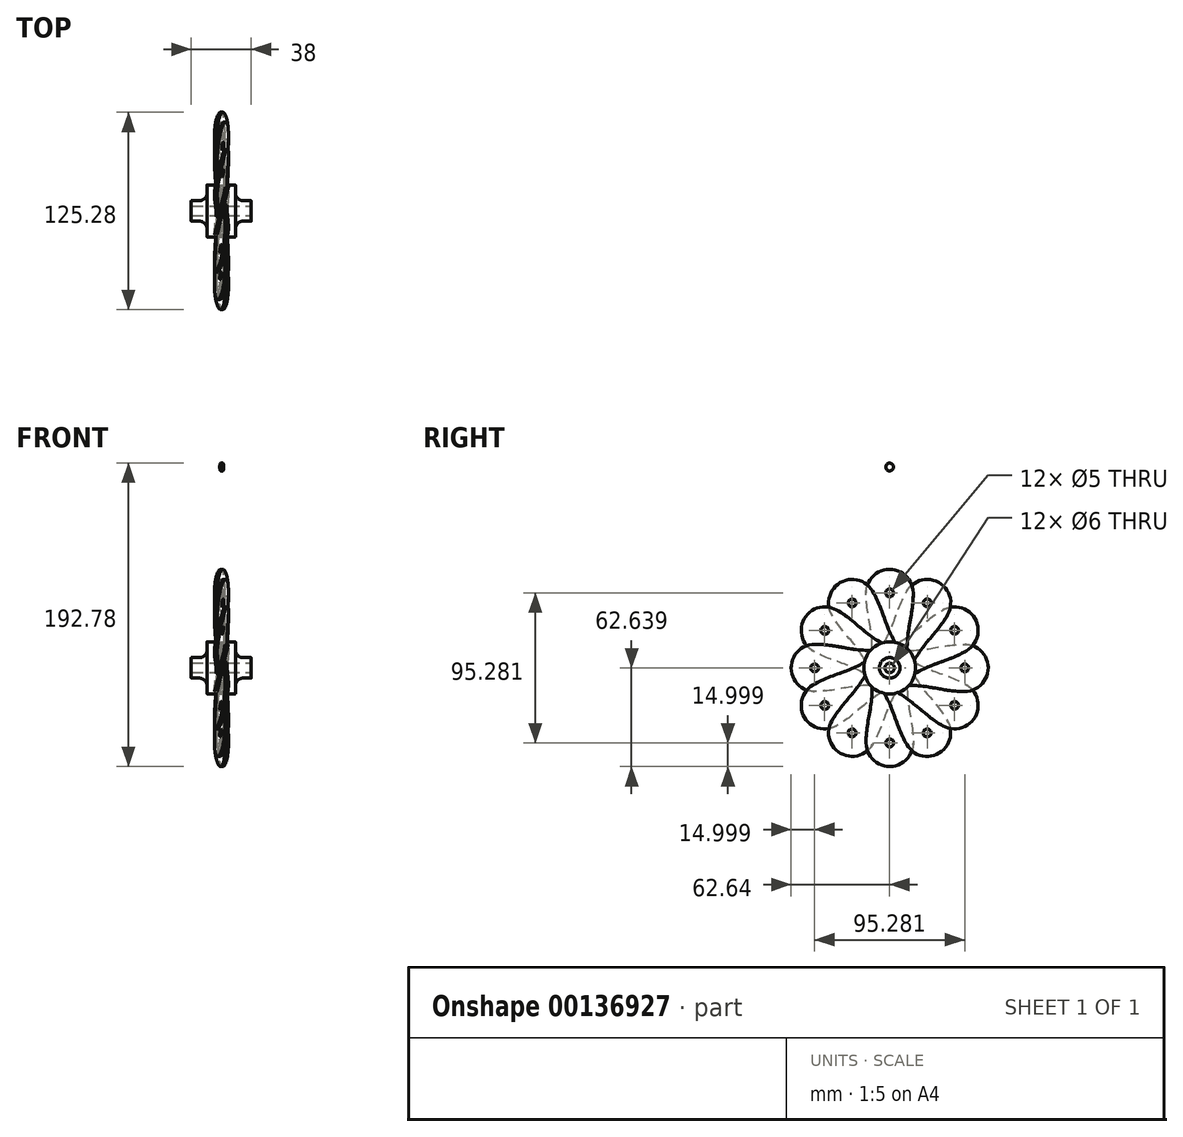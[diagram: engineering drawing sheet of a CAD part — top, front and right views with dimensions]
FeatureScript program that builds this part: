
annotation { "Feature Type Name" : "Feature", "Feature Type Description" : "" }
export const myFeature = defineFeature(function(context is Context, id is Id, definition is map)
    precondition{}
    {
        {
            var Q0;
            Q0=qCreatedBy(makeId("Right.planeOp"),FACE);
            var sketch = newSketch(context, id + "F0", { "sketchPlane" : qUnion([Q0])});
            skCircle(sketch, "E0", {"center": v(0, 0) * mm, "radius": 15 * mm});
            skCircle(sketch, "E1", {"center": v(0, -50) * mm, "radius": 12.5 * mm});
            skCircle(sketch, "E2", {"center": v(0, 80) * mm, "radius": 2.5 * mm});
            skCircle(sketch, "E3", {"center": v(0, 0) * mm, "radius": 2.5 * mm});
            skCircle(sketch, "E4.0.1.0", {"center": v(0, 25) * mm, "radius": 2.5 * mm});
            skCircle(sketch, "E4.0.2.0", {"center": v(0, 50) * mm, "radius": 2.5 * mm});
            skLineSegment(sketch, "E4.direction1", {"start": v(0, 0) * mm, "end": v(25, 0) * mm, "construction": true});
            skLineSegment(sketch, "E4.direction2", {"start": v(0, 0) * mm, "end": v(0, 25) * mm, "construction": true});
            skFitSpline(sketch, "E5", {"points": [v(-12.31, -47.84) * mm, v(-15, 0) * mm, v(-2.5, 80.18) * mm], "startDerivative": vector(26.28, 150.08) * mm, "endDerivative": vector(8.01, 113.17) * mm});
            skFitSpline(sketch, "E6.MirrorCS", {"points": [v(12.31, -47.84) * mm, v(15, 0) * mm, v(2.5, 80.18) * mm], "startDerivative": vector(-26.28, 150.08) * mm, "endDerivative": vector(-8.01, 113.17) * mm});
            skSolve(sketch);
        }
        {
            var Q0;
            {var subQ0=sQuery(id+"F0.wireOp",EDGE,"E5");var subQ1=sQuery(id+"F0.wireOp",EDGE,"E0");var subQ2=makeQuery(id+"F0.imprint","INTERSECT",VERTEX,{"derivedFrom":[subQ1,subQ0]});Q0=makeQuery(id+"F0.imprint","IMPRINT",FACE,{"disambiguationData":[TD([[makeQuery(id+"F0.imprint","IMPRINT",EDGE,{"disambiguationData":[TD([[subQ2,-1.0]])],"derivedFrom":subQ1}),-1.0]])]});}
            var Q1;
            Q1=makeQuery(id+"F0.imprint","IMPRINT",FACE,{"disambiguationData":[TD([[makeQuery(id+"F0.imprint","IMPRINT",EDGE,{"derivedFrom":sQuery(id+"F0.wireOp",EDGE,"E3")}),-1.0]])]});
            var Q2;
            Q2=makeQuery(id+"F0.imprint","IMPRINT",FACE,{"disambiguationData":[TD([[makeQuery(id+"F0.imprint","IMPRINT",EDGE,{"derivedFrom":sQuery(id+"F0.wireOp",EDGE,"E4.0.1.0")}),-1.0]])]});
            var Q3;
            {var subQ0=sQuery(id+"F0.wireOp",EDGE,"E2");var subQ1=makeQuery(id+"F0.imprint","INTERSECT",VERTEX,{"derivedFrom":[subQ0,sQuery(id+"F0.wireOp",EDGE,"E5")]});Q3=makeQuery(id+"F0.imprint","IMPRINT",FACE,{"disambiguationData":[TD([[makeQuery(id+"F0.imprint","IMPRINT",EDGE,{"disambiguationData":[TD([[subQ1,1.0]])],"derivedFrom":subQ0}),1.0]])]});}
            extrude(context, id + "F1", {"entities" : qUnion([Q0, Q1, Q2, Q3]), "depth" : 25 * mm});
        }
        {
            var Q0;
            Q0=qCreatedBy(makeId("Top.planeOp"),FACE);
            var sketch = newSketch(context, id + "F2", { "sketchPlane" : qUnion([Q0])});
            skLineSegment(sketch, "E7", {"start": v(0, -30.82) * mm, "end": v(0, 22.95) * mm});
            skLineSegment(sketch, "E8", {"start": v(0, 22.95) * mm, "end": v(12.68, 22.95) * mm});
            skLineSegment(sketch, "E9", {"start": v(-1.1, -41.33) * mm, "end": v(21.41, 54.16) * mm, "construction": true});
            skLineSegment(sketch, "E10.MirrorCS", {"start": v(15.28, 22.34) * mm, "end": v(2.6, -31.43) * mm});
            skLineSegment(sketch, "E11.MirrorCS", {"start": v(26.63, 16.67) * mm, "end": v(15.28, 22.34) * mm});
            skLineSegment(sketch, "E12", {"start": v(2.6, -31.43) * mm, "end": v(30.66, -22.66) * mm});
            skLineSegment(sketch, "E13", {"start": v(30.66, -22.66) * mm, "end": v(26.63, 16.67) * mm});
            skFitSpline(sketch, "E14", {"points": [v(0, -30.82) * mm, v(8.64, 0) * mm, v(12.68, 22.95) * mm], "startDerivative": vector(17.97, 59.07) * mm, "endDerivative": vector(7.1, 48.17) * mm});
            skSolve(sketch);
        }
        {
            var Q0;
            Q0=qSketchRegion(id+"F2",true);
            extrude(context, id + "F3", {"entities" : qUnion([Q0]), "operationType" : NewBodyOperationType.REMOVE, "oppositeDirection" : true, "depth" : 77 * mm, "hasSecondDirection" : true, "secondDirectionOppositeDirection" : false, "secondDirectionDepth" : 98.55 * mm});
        }
        {
            var Q0;
            Q0=makeQuery(id+"F3.boolean.opBoolean","INTERSECT",VERTEX,{"derivedFrom":[makeQuery(id+"F1.opExtrude","SWEPT_FACE",FACE,{"disambiguationData":[OSD([sQuery(id+"F0.wireOp",EDGE,"E1")])]}),makeQuery(id+"F1.opExtrude","SWEPT_FACE",FACE,{"disambiguationData":[OSD([sQuery(id+"F0.wireOp",EDGE,"E5")])]}),makeQuery(id+"F3.opExtrude","SWEPT_FACE",FACE,{"disambiguationData":[OSD([sQuery(id+"F2.wireOp",EDGE,"E10.MirrorCS")])]})]});
            var Q1;
            Q1=makeQuery(id+"F3.boolean.opBoolean","INTERSECT",VERTEX,{"derivedFrom":[makeQuery(id+"F1.opExtrude","SWEPT_FACE",FACE,{"disambiguationData":[OSD([sQuery(id+"F0.wireOp",EDGE,"E1")])]}),makeQuery(id+"F1.opExtrude","SWEPT_FACE",FACE,{"disambiguationData":[OSD([sQuery(id+"F0.wireOp",EDGE,"E6.MirrorCS")])]}),makeQuery(id+"F3.opExtrude","SWEPT_FACE",FACE,{"disambiguationData":[OSD([sQuery(id+"F2.wireOp",EDGE,"E10.MirrorCS")])]})]});
            var Q2;
            Q2=makeQuery(id+"F3.boolean.opBoolean","INTERSECT",VERTEX,{"derivedFrom":[makeQuery(id+"F1.opExtrude","SWEPT_FACE",FACE,{"disambiguationData":[OSD([sQuery(id+"F0.wireOp",EDGE,"E1")])]}),makeQuery(id+"F1.opExtrude","SWEPT_FACE",FACE,{"disambiguationData":[OSD([sQuery(id+"F0.wireOp",EDGE,"E6.MirrorCS")])]}),makeQuery(id+"F3.opExtrude","SWEPT_FACE",FACE,{"disambiguationData":[OSD([sQuery(id+"F2.wireOp",EDGE,"E14")])]})]});
            cPlane(context, id + "F4", {"entities" : qUnion([Q0, Q1, Q2]), "cplaneType" : CPlaneType.THREE_POINT, "offset" : 25 * mm, "width" : 150 * mm, "height" : 150 * mm});
        }
        {
            var Q0;
            Q0=qCreatedBy(id+"F4.planeOp",FACE);
            var sketch = newSketch(context, id + "F5", { "sketchPlane" : qUnion([Q0])});
            skLineSegment(sketch, "E15", {"start": v(66.32, 0) * mm, "end": v(-28.05, 0) * mm, "construction": true});
            skLineSegment(sketch, "E16", {"start": v(28, 3) * mm, "end": v(-10, 3) * mm});
            skLineSegment(sketch, "E17", {"start": v(-10, 3) * mm, "end": v(-10, 6.5) * mm});
            skLineSegment(sketch, "E18", {"start": v(-10, 6.5) * mm, "end": v(-5, 6.5) * mm});
            skLineSegment(sketch, "E19", {"start": v(0, 11.5) * mm, "end": v(0, 16.5) * mm});
            skLineSegment(sketch, "E20", {"start": v(0, 16.5) * mm, "end": v(18, 16.5) * mm});
            skLineSegment(sketch, "E21", {"start": v(18, 16.5) * mm, "end": v(18, 11.5) * mm});
            skLineSegment(sketch, "E22", {"start": v(23, 6.5) * mm, "end": v(28, 6.5) * mm});
            skLineSegment(sketch, "E23", {"start": v(28, 6.5) * mm, "end": v(28, 3) * mm});
            skPoint(sketch, "E24.visualSharp", {"position": v(18, 6.5) * mm});
            skArc(sketch, "E24.filletArc", {"start": v(18, 11.5) * mm, "mid": v(19.46, 7.96) * mm, "end": v(23, 6.5) * mm});
            skPoint(sketch, "E25.visualSharp", {"position": v(0, 6.5) * mm});
            skArc(sketch, "E25.filletArc", {"start": v(-5, 6.5) * mm, "mid": v(-1.46, 7.96) * mm, "end": v(0, 11.5) * mm});
            skSolve(sketch);
        }
        {
            var Q0;
            Q0=makeQuery(id+"F5.imprint","IMPRINT",FACE,{"disambiguationData":[TD([[makeQuery(id+"F5.imprint","IMPRINT",EDGE,{"derivedFrom":sQuery(id+"F5.wireOp",EDGE,"E16")}),-1.0]])]});
            var Q1;
            Q1=sQuery(id+"F5.wireOp",EDGE,"E15");
            revolve(context, id + "F6", {"operationType" : NewBodyOperationType.ADD, "entities" : qUnion([Q0]), "axis" : qUnion([Q1]), "revolveType" : RevolveType.FULL});
        }
        {
            var Q0;
            Q0=makeQuery(id+"F1.opExtrude","SWEPT_BODY",BODY,{"disambiguationData":[OSD([sQuery(id+"F0.wireOp",EDGE,"E1"),sQuery(id+"F0.wireOp",EDGE,"E2"),sQuery(id+"F0.wireOp",EDGE,"E3"),sQuery(id+"F0.wireOp",EDGE,"E4.0.1.0"),sQuery(id+"F0.wireOp",EDGE,"E4.0.2.0"),sQuery(id+"F0.wireOp",EDGE,"E5"),sQuery(id+"F0.wireOp",EDGE,"E6.MirrorCS")])]});
            var Q1;
            Q1=makeQuery(id+"F6.opRevolve","SWEPT_EDGE",EDGE,{"disambiguationData":[OSD([sQuery(id+"F5.wireOp",EDGE,"E16"),sQuery(id+"F5.wireOp",EDGE,"E23")])]});
            circularPattern(context, id + "F7", {"operationType" : NewBodyOperationType.ADD, "entities" : qUnion([Q0]), "axis" : qUnion([Q1]), "angle" : 30 * degree, "instanceCount" : 12});
        }
    });
